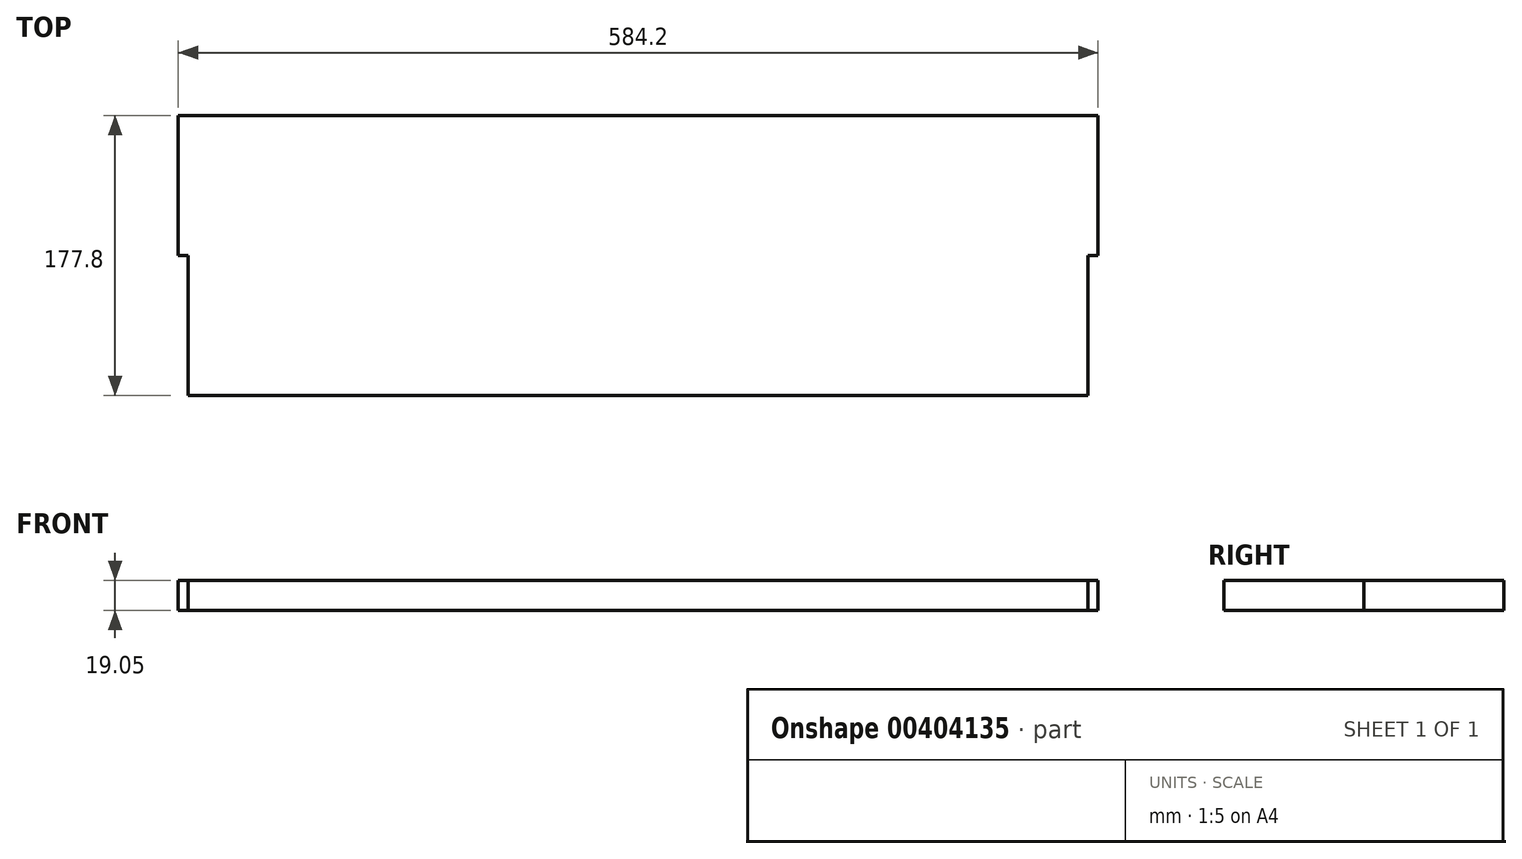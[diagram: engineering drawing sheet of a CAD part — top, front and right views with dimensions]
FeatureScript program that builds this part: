
annotation { "Feature Type Name" : "Feature", "Feature Type Description" : "" }
export const myFeature = defineFeature(function(context is Context, id is Id, definition is map)
    precondition{}
    {
        {
            var Q0;
            Q0=qCreatedBy(makeId("Front.planeOp"),FACE);
            var sketch = newSketch(context, id + "F0", { "sketchPlane" : qUnion([Q0])});
            skLineSegment(sketch, "E0.bottom", {"start": v(0, 0) * mm, "end": v(571.5, 0) * mm});
            skLineSegment(sketch, "E0.top", {"start": v(0, 19.05) * mm, "end": v(571.5, 19.05) * mm});
            skLineSegment(sketch, "E0.left", {"start": v(0, 0) * mm, "end": v(0, 19.05) * mm});
            skLineSegment(sketch, "E0.right", {"start": v(571.5, 0) * mm, "end": v(571.5, 19.05) * mm});
            skSolve(sketch);
        }
        {
            var Q0;
            Q0 = qSketchRegion(id + "F0", true);
            extrude(context, id + "F1", {"entities" : qUnion([Q0]), "endBound" : BoundingType.SYMMETRIC, "depth" : 177.8 * mm});
        }
        {
            var Q0;
            Q0=makeQuery(id+"F1.opExtrude","SWEPT_FACE",FACE,{"disambiguationData":[OSD([sQuery(id+"F0.wireOp",EDGE,"E0.right")])]});
            var sketch = newSketch(context, id + "F2", { "sketchPlane" : qUnion([Q0])});
            skLineSegment(sketch, "E1.bottom", {"start": v(0, 0) * mm, "end": v(88.9, 0) * mm});
            skLineSegment(sketch, "E1.top", {"start": v(0, 19.05) * mm, "end": v(88.9, 19.05) * mm});
            skLineSegment(sketch, "E1.left", {"start": v(0, 0) * mm, "end": v(0, 19.05) * mm});
            skLineSegment(sketch, "E1.right", {"start": v(88.9, 0) * mm, "end": v(88.9, 19.05) * mm});
            skSolve(sketch);
        }
        {
            var Q0;
            Q0 = qSketchRegion(id + "F2", true);
            extrude(context, id + "F3", {"entities" : qUnion([Q0]), "operationType" : NewBodyOperationType.ADD, "depth" : 6.35 * mm});
        }
        {
            var Q0;
            Q0=makeQuery(id+"F1.opExtrude","SWEPT_FACE",FACE,{"disambiguationData":[OSD([sQuery(id+"F0.wireOp",EDGE,"E0.left")])]});
            var sketch = newSketch(context, id + "F4", { "sketchPlane" : qUnion([Q0])});
            skLineSegment(sketch, "E2.bottom", {"start": v(0, 0) * mm, "end": v(-88.9, 0) * mm});
            skLineSegment(sketch, "E2.top", {"start": v(0, 19.05) * mm, "end": v(-88.9, 19.05) * mm});
            skLineSegment(sketch, "E2.left", {"start": v(0, 0) * mm, "end": v(0, 19.05) * mm});
            skLineSegment(sketch, "E2.right", {"start": v(-88.9, 0) * mm, "end": v(-88.9, 19.05) * mm});
            skSolve(sketch);
        }
        {
            var Q0;
            Q0 = qSketchRegion(id + "F4", true);
            extrude(context, id + "F5", {"entities" : qUnion([Q0]), "operationType" : NewBodyOperationType.ADD, "depth" : 6.35 * mm, "hasSecondDirection" : true, "secondDirectionOppositeDirection" : true, "secondDirectionDepth" : 25.4 * mm});
        }
    });
